# Revit family: IP АТС «Аэлита-1050»_RV17_LOD400
name_source: partatom
category: Электрооборудование
revit_build: Autodesk Revit 2017 (Build: 20170118_1100(x64)
units: mm (PartAtom-declared; Revit-internal decimal feet)

## family parameters
Всегда вертикально = Нет
Конфигурация панели = Два столбца, слева направо
На основе рабочей плоскости = Нет
Общий = Нет
При загрузке вырезать с полостями = Нет
Размер круглого соединителя = Использовать диаметр
Тип детали = Щит
Точка расчета площади = Нет

## types (1)
- IP АТС «Аэлита-1050»
    ADSK_URL страницы изделия = https://stilsoft.ru
    ADSK_Единица измерения = шт.
    ADSK_Завод-изготовитель = ООО «Основа Безопасности»
    ADSK_Количество = 1
    ADSK_Марка = СТВФ.431295.008
    ADSK_Масса = 10
    ADSK_Наименование = IP АТС «АЭЛИТА-1050»
    ADSK_Размер_Высота = 89 мм
    ADSK_Размер_Длина = 533 мм
    ADSK_Размер_Ширина = 430 мм
    d_короба = 20 мм
    Время приведения в рабочее состояние не более, мин. = 2
    Диапазон рабочих температур, <unrecoverable-encoding: 5 bytes ef82b0d0a1> = от +5 до +50
    Максимальное количество подключаемых IP телефонов, шт. = 50
    Мощность = 135
    Напряжение = 220
    Поддержка работы нескольких IT АТС в сети = да
    Ресурс до профилактического обслуживания не менее, ч = 4400
